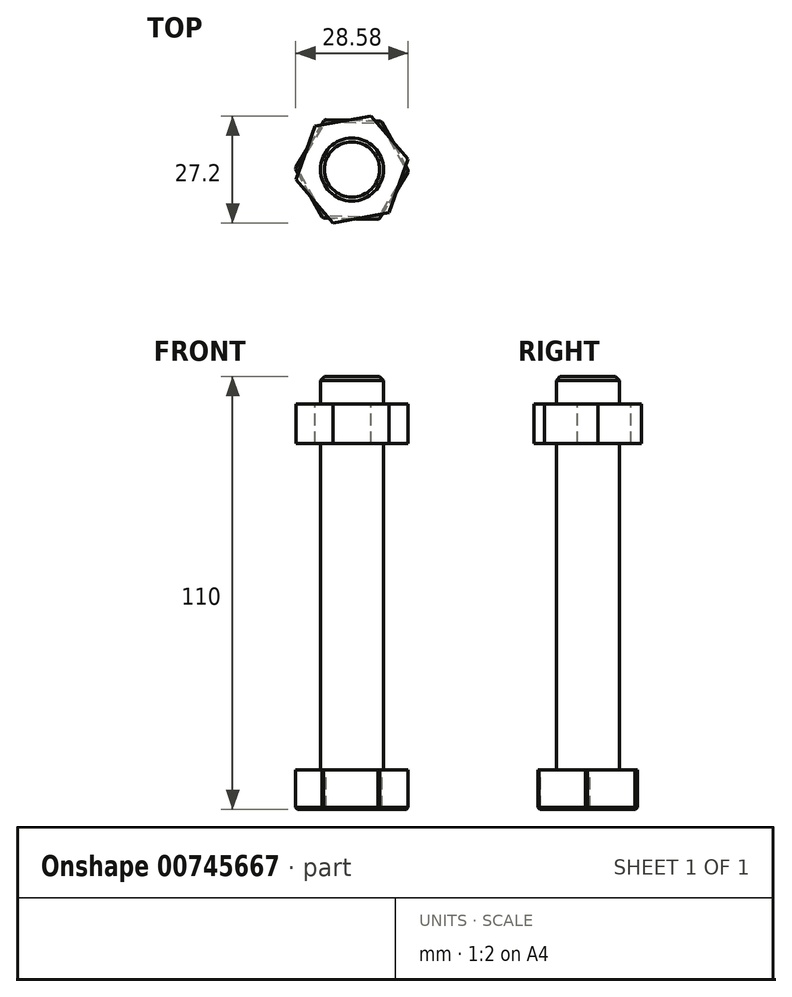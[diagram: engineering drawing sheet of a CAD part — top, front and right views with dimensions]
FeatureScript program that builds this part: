
annotation { "Feature Type Name" : "Feature", "Feature Type Description" : "" }
export const myFeature = defineFeature(function(context is Context, id is Id, definition is map)
    precondition{}
    {
        {
            var Q0;
            Q0=qCreatedBy(makeId("Top.planeOp"),FACE);
            var sketch = newSketch(context, id + "F0", { "sketchPlane" : qUnion([Q0])});
            skCircle(sketch, "E0.cCircle", {"center": v(0, 0) * mm, "radius": 12.5 * mm, "construction": true});
            skLineSegment(sketch, "E0.0", {"start": v(-7.53, -12.31) * mm, "end": v(-14.43, 0.36) * mm});
            skLineSegment(sketch, "E0.1", {"start": v(-14.43, 0.36) * mm, "end": v(-6.9, 12.68) * mm});
            skLineSegment(sketch, "E0.2", {"start": v(-6.9, 12.68) * mm, "end": v(7.53, 12.31) * mm});
            skLineSegment(sketch, "E0.3", {"start": v(7.53, 12.31) * mm, "end": v(14.43, -0.36) * mm});
            skLineSegment(sketch, "E0.4", {"start": v(14.43, -0.36) * mm, "end": v(6.9, -12.68) * mm});
            skLineSegment(sketch, "E0.5", {"start": v(6.9, -12.68) * mm, "end": v(-7.53, -12.31) * mm});
            skPoint(sketch, "E0.0.midPoint", {"position": v(-10.98, -5.97) * mm});
            skSolve(sketch);
        }
        {
            var Q0;
            Q0=makeQuery(id+"F0.imprint","IMPRINT",FACE,{"disambiguationData":[TD([[makeQuery(id+"F0.imprint","IMPRINT",EDGE,{"derivedFrom":sQuery(id+"F0.wireOp",EDGE,"E0.0")}),-1.0]])]});
            extrude(context, id + "F1", {"entities" : qUnion([Q0]), "depth" : 10 * mm, "offsetDistance" : 25 * mm});
        }
        {
            var Q0;
            Q0=makeQuery(id+"F1.opExtrude","CAP_FACE",FACE,{"disambiguationData":[OSD([sQuery(id+"F0.wireOp",EDGE,"E0.0"),sQuery(id+"F0.wireOp",EDGE,"E0.1"),sQuery(id+"F0.wireOp",EDGE,"E0.2"),sQuery(id+"F0.wireOp",EDGE,"E0.3"),sQuery(id+"F0.wireOp",EDGE,"E0.4"),sQuery(id+"F0.wireOp",EDGE,"E0.5")])],"isStart":false});
            var sketch = newSketch(context, id + "F2", { "sketchPlane" : qUnion([Q0])});
            skCircle(sketch, "E1", {"center": v(0, 0) * mm, "radius": 8 * mm});
            skSolve(sketch);
        }
        {
            var Q0;
            Q0=makeQuery(id+"F2.imprint","IMPRINT",FACE,{"disambiguationData":[TD([[makeQuery(id+"F2.imprint","IMPRINT",EDGE,{"derivedFrom":sQuery(id+"F2.wireOp",EDGE,"E1")}),1.0]])]});
            extrude(context, id + "F3", {"entities" : qUnion([Q0]), "operationType" : NewBodyOperationType.ADD, "depth" : 100 * mm, "offsetDistance" : 25 * mm});
        }
        {
            var Q0;
            Q0=makeQuery(id+"F3.opExtrude","CAP_FACE",FACE,{"disambiguationData":[OSD([sQuery(id+"F2.wireOp",EDGE,"E1")])],"isStart":false});
            cPlane(context, id + "F4", {"entities" : qUnion([Q0]), "cplaneType" : CPlaneType.OFFSET, "offset" : 7 * mm, "oppositeDirection" : true, "width" : 150 * mm, "height" : 150 * mm});
        }
        {
            var Q0;
            Q0=qCreatedBy(id+"F4.planeOp",FACE);
            var sketch = newSketch(context, id + "F5", { "sketchPlane" : qUnion([Q0])});
            skCircle(sketch, "E2.cCircle", {"center": v(0, 0) * mm, "radius": 12.5 * mm, "construction": true});
            skLineSegment(sketch, "E2.0", {"start": v(14.2, 2.6) * mm, "end": v(9.35, -11) * mm});
            skLineSegment(sketch, "E2.1", {"start": v(9.35, -11) * mm, "end": v(-4.85, -13.6) * mm});
            skLineSegment(sketch, "E2.2", {"start": v(-4.85, -13.6) * mm, "end": v(-14.2, -2.6) * mm});
            skLineSegment(sketch, "E2.3", {"start": v(-14.2, -2.6) * mm, "end": v(-9.35, 11) * mm});
            skLineSegment(sketch, "E2.4", {"start": v(-9.35, 11) * mm, "end": v(4.85, 13.6) * mm});
            skLineSegment(sketch, "E2.5", {"start": v(4.85, 13.6) * mm, "end": v(14.2, 2.6) * mm});
            skPoint(sketch, "E2.0.midPoint", {"position": v(11.77, -4.2) * mm});
            skSolve(sketch);
        }
        {
            var Q0;
            Q0 = qSketchRegion(id + "F5", true);
            extrude(context, id + "F6", {"entities" : qUnion([Q0]), "operationType" : NewBodyOperationType.ADD, "oppositeDirection" : true, "depth" : 10 * mm, "offsetDistance" : 25 * mm});
        }
        {
            var Q0;
            Q0=makeQuery(id+"F3.opExtrude","CAP_EDGE",EDGE,{"disambiguationData":[OSD([sQuery(id+"F2.wireOp",EDGE,"E1")])],"isStart":false});
            chamfer(context, id + "F7", {"entities" : qUnion([Q0]), "width" : 1 * mm, "tangentPropagation" : true});
        }
        {
            var Q0;
            Q0=makeQuery(id+"F1.opExtrude","CAP_FACE",FACE,{"disambiguationData":[OSD([sQuery(id+"F0.wireOp",EDGE,"E0.0"),sQuery(id+"F0.wireOp",EDGE,"E0.1"),sQuery(id+"F0.wireOp",EDGE,"E0.2"),sQuery(id+"F0.wireOp",EDGE,"E0.3"),sQuery(id+"F0.wireOp",EDGE,"E0.4"),sQuery(id+"F0.wireOp",EDGE,"E0.5")])],"isStart":true});
            var Q1;
            Q1=makeQuery(id+"F1.opExtrude","SWEPT_EDGE",EDGE,{"disambiguationData":[OSD([sQuery(id+"F0.wireOp",EDGE,"E0.0"),sQuery(id+"F0.wireOp",EDGE,"E0.5")])]});
            var Q2;
            Q2=makeQuery(id+"F1.opExtrude","SWEPT_EDGE",EDGE,{"disambiguationData":[OSD([sQuery(id+"F0.wireOp",EDGE,"E0.4"),sQuery(id+"F0.wireOp",EDGE,"E0.5")])]});
            var Q3;
            Q3=makeQuery(id+"F1.opExtrude","SWEPT_EDGE",EDGE,{"disambiguationData":[OSD([sQuery(id+"F0.wireOp",EDGE,"E0.3"),sQuery(id+"F0.wireOp",EDGE,"E0.4")])]});
            var Q4;
            Q4=makeQuery(id+"F1.opExtrude","SWEPT_EDGE",EDGE,{"disambiguationData":[OSD([sQuery(id+"F0.wireOp",EDGE,"E0.2"),sQuery(id+"F0.wireOp",EDGE,"E0.3")])]});
            var Q5;
            Q5=makeQuery(id+"F1.opExtrude","SWEPT_EDGE",EDGE,{"disambiguationData":[OSD([sQuery(id+"F0.wireOp",EDGE,"E0.1"),sQuery(id+"F0.wireOp",EDGE,"E0.2")])]});
            var Q6;
            Q6=makeQuery(id+"F1.opExtrude","SWEPT_EDGE",EDGE,{"disambiguationData":[OSD([sQuery(id+"F0.wireOp",EDGE,"E0.0"),sQuery(id+"F0.wireOp",EDGE,"E0.1")])]});
            chamfer(context, id + "F8", {"entities" : qUnion([Q0, Q1, Q2, Q3, Q4, Q5, Q6]), "width" : 0.5 * mm, "tangentPropagation" : true});
        }
    });
